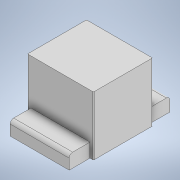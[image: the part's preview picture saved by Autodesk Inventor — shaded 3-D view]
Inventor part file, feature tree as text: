
AUTODESK INVENTOR PART (.ipt)
format: ipt  version: 2022 (Build 260153000, 153)  size: 132,608 bytes
history: native  units: in
note: dims shown in document units (in); Inventor stores cm internally (conversion verified against a paired STEP export)
features: fillet x6, sketch x3, extrude x2, mirror x1
ambient origin geometry x8: Origin, YZ Plane, XZ Plane, XY Plane, X Axis, Y Axis, Z Axis, Center Point
bodies: Solid1 (feature_tree)
feature tree (12):
  extrude  "Extrusion1"  Depth=3.3465in
  fillet  "Face Fillet1"
  fillet  "Face Fillet2"
  fillet  "Face Fillet3"
  fillet  "Face Fillet4"
  extrude  "Extrusion2"  Depth=0.0394in
  mirror  "Mirror1"
  fillet  "Face Fillet5"
  fillet  "Face Fillet6"
  sketch  "Sketch3"  dims[d5=0.0394in d6=0.0394in d7=0.0394in d9=0.7874in d10=3.3465in d11=1.1811in d12=0.0in d13=0.1969in d14=0.1969in]
  sketch  "Sketch1"  dims[d0=3.7402in d1=3.3465in]
  sketch  "Sketch2"  dims[d2=3.3465in d3=0.0in d4=0.0394in]
